annotation { "Feature Type Name" : "Feature", "Feature Type Description" : "" }
export const myFeature = defineFeature(function(context is Context, id is Id, definition is map)
    precondition{}
    {
        {
            var Q0;
            Q0=qCreatedBy(makeId("Top.planeOp"),FACE);
            var sketch = newSketch(context, id + "F0", { "sketchPlane" : qUnion([Q0])});
            skLineSegment(sketch, "E0.bottom", {"start": v(31.75, 56.17) * mm, "end": v(-31.75, 56.17) * mm});
            skLineSegment(sketch, "E0.top", {"start": v(31.75, -56.16) * mm, "end": v(-31.75, -56.16) * mm});
            skLineSegment(sketch, "E0.left", {"start": v(31.75, 56.17) * mm, "end": v(31.75, -56.16) * mm});
            skLineSegment(sketch, "E0.right", {"start": v(-31.75, 56.17) * mm, "end": v(-31.75, -56.16) * mm});
            skPoint(sketch, "E0.middle", {"position": v(0, 0) * mm});
            skCircle(sketch, "E1", {"center": v(0, 33.22) * mm, "radius": 0.46 * mm});
            skLineSegment(sketch, "E2", {"start": v(-15.68, -20.06) * mm, "end": v(-13.05, -16.82) * mm});
            skLineSegment(sketch, "E3", {"start": v(-4.55, -6.35) * mm, "end": v(-4.14, -13.2) * mm});
            skLineSegment(sketch, "E4", {"start": v(-2.74, -36.1) * mm, "end": v(-9.1, -24.2) * mm});
            skLineSegment(sketch, "E5", {"start": v(-20.85, -2.21) * mm, "end": v(7.08, -20.58) * mm});
            skLineSegment(sketch, "E6", {"start": v(7.08, -20.58) * mm, "end": v(-3.54, -22.95) * mm});
            skLineSegment(sketch, "E7", {"start": v(-19.56, -26.53) * mm, "end": v(-15.68, -20.06) * mm});
            skPoint(sketch, "E8.endSnap0", {"position": v(-21.88, 4.12) * mm});
            skLineSegment(sketch, "E9", {"start": v(8.64, -42.82) * mm, "end": v(10.26, -40.5) * mm});
            skLineSegment(sketch, "E10", {"start": v(18.2, -29.11) * mm, "end": v(18.76, -34.8) * mm});
            skLineSegment(sketch, "E11", {"start": v(20.53, -52.9) * mm, "end": v(12.96, -43.77) * mm});
            skLineSegment(sketch, "E12", {"start": v(5.53, -34.8) * mm, "end": v(14.23, -34.8) * mm});
            skLineSegment(sketch, "E13", {"start": v(27.52, -34.8) * mm, "end": v(19.26, -39.9) * mm});
            skLineSegment(sketch, "E14", {"start": v(5.27, -48.51) * mm, "end": v(8.64, -42.82) * mm});
            skText(sketch, "E15", { "text": "QUEEN JANELLE", "fontName": "OpenSans-Regular.ttf"});
            skCircle(sketch, "E16", {"center": v(0, 40.72) * mm, "radius": 7.79 * mm});
            skPoint(sketch, "E17.orphan", {"position": v(-7.14, 4.12) * mm});
            skPoint(sketch, "E18.orphan", {"position": v(-14.42, 0) * mm});
            skPoint(sketch, "E19.orphan", {"position": v(-27.32, -1.7) * mm});
            skPoint(sketch, "E20.start.orphan", {"position": v(-16.45, 9.94) * mm});
            skLineSegment(sketch, "E21", {"start": v(-27.32, -1.7) * mm, "end": v(-21.88, 4.12) * mm});
            skLineSegment(sketch, "E22", {"start": v(-16.45, 9.94) * mm, "end": v(-15.92, 6.43) * mm});
            skLineSegment(sketch, "E23", {"start": v(-14.42, -3.5) * mm, "end": v(-18.7, 0.79) * mm});
            skLineSegment(sketch, "E24", {"start": v(-27.32, 9.43) * mm, "end": v(-18.98, 7.23) * mm});
            skLineSegment(sketch, "E25", {"start": v(-27.32, -1.7) * mm, "end": v(-18.7, 0.79) * mm});
            skLineSegment(sketch, "E26", {"start": v(9.41, -6.35) * mm, "end": v(11.7, -1.56) * mm});
            skLineSegment(sketch, "E27", {"start": v(16.91, 9.43) * mm, "end": v(18.6, 4.51) * mm});
            skLineSegment(sketch, "E28", {"start": v(24.41, -12.3) * mm, "end": v(14, -3.51) * mm});
            skLineSegment(sketch, "E29", {"start": v(4.5, 4.51) * mm, "end": v(14.58, 4.51) * mm});
            skLineSegment(sketch, "E30", {"start": v(27, 4.51) * mm, "end": v(20.08, 0.24) * mm});
            skLineSegment(sketch, "E31.trimOffspring", {"start": v(-18.98, 7.23) * mm, "end": v(-16.45, 9.94) * mm});
            skLineSegment(sketch, "E32.trimOffspring", {"start": v(-15.92, 6.43) * mm, "end": v(-7.14, 4.12) * mm});
            skLineSegment(sketch, "E33.trimOffspring", {"start": v(-15.22, 1.8) * mm, "end": v(-14.42, -3.5) * mm});
            skLineSegment(sketch, "E34.trimOffspring", {"start": v(-15.22, 1.8) * mm, "end": v(-7.14, 4.12) * mm});
            skLineSegment(sketch, "E35.trimOffspring", {"start": v(-21.95, 4.05) * mm, "end": v(-27.32, 9.43) * mm});
            skLineSegment(sketch, "E36.trimOffspring", {"start": v(-13.05, -16.82) * mm, "end": v(-20.85, -2.21) * mm});
            skLineSegment(sketch, "E37.trimOffspring", {"start": v(-8.03, -10.64) * mm, "end": v(-4.55, -6.35) * mm});
            skLineSegment(sketch, "E38.trimOffspring", {"start": v(-3.54, -22.95) * mm, "end": v(-2.74, -36.1) * mm});
            skLineSegment(sketch, "E39.trimOffspring", {"start": v(-9.1, -24.2) * mm, "end": v(-19.56, -26.53) * mm});
            skLineSegment(sketch, "E40.trimOffspring", {"start": v(14.23, -34.8) * mm, "end": v(18.2, -29.11) * mm});
            skLineSegment(sketch, "E41.trimOffspring", {"start": v(18.76, -34.8) * mm, "end": v(27.52, -34.8) * mm});
            skLineSegment(sketch, "E42.trimOffspring", {"start": v(19.26, -39.9) * mm, "end": v(20.53, -52.9) * mm});
            skLineSegment(sketch, "E43.trimOffspring", {"start": v(12.96, -43.77) * mm, "end": v(5.27, -48.51) * mm});
            skLineSegment(sketch, "E44.trimOffspring", {"start": v(10.26, -40.5) * mm, "end": v(5.53, -34.8) * mm});
            skLineSegment(sketch, "E45.trimOffspring", {"start": v(14, -3.51) * mm, "end": v(9.41, -6.35) * mm});
            skLineSegment(sketch, "E46.trimOffspring", {"start": v(18.6, 4.51) * mm, "end": v(27, 4.51) * mm});
            skLineSegment(sketch, "E47.trimOffspring", {"start": v(14.58, 4.51) * mm, "end": v(16.91, 9.43) * mm});
            skLineSegment(sketch, "E48.trimOffspring", {"start": v(20.08, 0.24) * mm, "end": v(24.41, -12.3) * mm});
            skLineSegment(sketch, "E49.trimOffspring", {"start": v(11.7, -1.56) * mm, "end": v(4.5, 4.51) * mm});
            const initialGuessF0  = {"E15": [-0.02986, 0.0172, 1, 0, 0.00585]};
            skSetInitialGuess(sketch, initialGuessF0);
            skSolve(sketch);
        }
        {
            var Q0;
            Q0 = qSketchRegion(id + "F0", true);
            extrude(context, id + "F1", {"entities" : qUnion([Q0]), "depth" : 2 * mm});
        }
        {
            var Q0;
            Q0=makeQuery(id+"F1.opExtrude","CAP_FACE",FACE,{"disambiguationData":[OSD([sQuery(id+"F0.wireOp",EDGE,"E0.bottom"),sQuery(id+"F0.wireOp",EDGE,"E0.top"),sQuery(id+"F0.wireOp",EDGE,"E0.left"),sQuery(id+"F0.wireOp",EDGE,"E0.right"),sQuery(id+"F0.wireOp",EDGE,"E1"),sQuery(id+"F0.wireOp",EDGE,"E2"),sQuery(id+"F0.wireOp",EDGE,"E3"),sQuery(id+"F0.wireOp",EDGE,"E4"),sQuery(id+"F0.wireOp",EDGE,"E5"),sQuery(id+"F0.wireOp",EDGE,"E6"),sQuery(id+"F0.wireOp",EDGE,"E7"),sQuery(id+"F0.wireOp",EDGE,"E9"),sQuery(id+"F0.wireOp",EDGE,"E10"),sQuery(id+"F0.wireOp",EDGE,"E11"),sQuery(id+"F0.wireOp",EDGE,"E12"),sQuery(id+"F0.wireOp",EDGE,"E13"),sQuery(id+"F0.wireOp",EDGE,"E14"),sQuery(id+"F0.wireOp",EDGE,"E15.sketch_text.stroke-0"),sQuery(id+"F0.wireOp",EDGE,"E15.sketch_text.stroke-1"),sQuery(id+"F0.wireOp",EDGE,"E15.sketch_text.stroke-2"),sQuery(id+"F0.wireOp",EDGE,"E15.sketch_text.stroke-3"),sQuery(id+"F0.wireOp",EDGE,"E15.sketch_text.stroke-4"),sQuery(id+"F0.wireOp",EDGE,"E15.sketch_text.stroke-5"),sQuery(id+"F0.wireOp",EDGE,"E15.sketch_text.stroke-6"),sQuery(id+"F0.wireOp",EDGE,"E15.sketch_text.stroke-7"),sQuery(id+"F0.wireOp",EDGE,"E15.sketch_text.stroke-8"),sQuery(id+"F0.wireOp",EDGE,"E15.sketch_text.stroke-9"),sQuery(id+"F0.wireOp",EDGE,"E15.sketch_text.stroke-10"),sQuery(id+"F0.wireOp",EDGE,"E15.sketch_text.stroke-11"),sQuery(id+"F0.wireOp",EDGE,"E15.sketch_text.stroke-20"),sQuery(id+"F0.wireOp",EDGE,"E15.sketch_text.stroke-21"),sQuery(id+"F0.wireOp",EDGE,"E15.sketch_text.stroke-22"),sQuery(id+"F0.wireOp",EDGE,"E15.sketch_text.stroke-23"),sQuery(id+"F0.wireOp",EDGE,"E15.sketch_text.stroke-24"),sQuery(id+"F0.wireOp",EDGE,"E15.sketch_text.stroke-25"),sQuery(id+"F0.wireOp",EDGE,"E15.sketch_text.stroke-26"),sQuery(id+"F0.wireOp",EDGE,"E15.sketch_text.stroke-27"),sQuery(id+"F0.wireOp",EDGE,"E15.sketch_text.stroke-28"),sQuery(id+"F0.wireOp",EDGE,"E15.sketch_text.stroke-29"),sQuery(id+"F0.wireOp",EDGE,"E15.sketch_text.stroke-30"),sQuery(id+"F0.wireOp",EDGE,"E15.sketch_text.stroke-31"),sQuery(id+"F0.wireOp",EDGE,"E15.sketch_text.stroke-32"),sQuery(id+"F0.wireOp",EDGE,"E15.sketch_text.stroke-33"),sQuery(id+"F0.wireOp",EDGE,"E15.sketch_text.stroke-34"),sQuery(id+"F0.wireOp",EDGE,"E15.sketch_text.stroke-35"),sQuery(id+"F0.wireOp",EDGE,"E15.sketch_text.stroke-36"),sQuery(id+"F0.wireOp",EDGE,"E15.sketch_text.stroke-37"),sQuery(id+"F0.wireOp",EDGE,"E15.sketch_text.stroke-38"),sQuery(id+"F0.wireOp",EDGE,"E15.sketch_text.stroke-39"),sQuery(id+"F0.wireOp",EDGE,"E15.sketch_text.stroke-40"),sQuery(id+"F0.wireOp",EDGE,"E15.sketch_text.stroke-41"),sQuery(id+"F0.wireOp",EDGE,"E15.sketch_text.stroke-42"),sQuery(id+"F0.wireOp",EDGE,"E15.sketch_text.stroke-43"),sQuery(id+"F0.wireOp",EDGE,"E15.sketch_text.stroke-44"),sQuery(id+"F0.wireOp",EDGE,"E15.sketch_text.stroke-45"),sQuery(id+"F0.wireOp",EDGE,"E15.sketch_text.stroke-46"),sQuery(id+"F0.wireOp",EDGE,"E15.sketch_text.stroke-47"),sQuery(id+"F0.wireOp",EDGE,"E15.sketch_text.stroke-48"),sQuery(id+"F0.wireOp",EDGE,"E15.sketch_text.stroke-49"),sQuery(id+"F0.wireOp",EDGE,"E15.sketch_text.stroke-50"),sQuery(id+"F0.wireOp",EDGE,"E15.sketch_text.stroke-51"),sQuery(id+"F0.wireOp",EDGE,"E15.sketch_text.stroke-52"),sQuery(id+"F0.wireOp",EDGE,"E15.sketch_text.stroke-53"),sQuery(id+"F0.wireOp",EDGE,"E15.sketch_text.stroke-54"),sQuery(id+"F0.wireOp",EDGE,"E15.sketch_text.stroke-55"),sQuery(id+"F0.wireOp",EDGE,"E15.sketch_text.stroke-56"),sQuery(id+"F0.wireOp",EDGE,"E15.sketch_text.stroke-57"),sQuery(id+"F0.wireOp",EDGE,"E15.sketch_text.stroke-58"),sQuery(id+"F0.wireOp",EDGE,"E15.sketch_text.stroke-59"),sQuery(id+"F0.wireOp",EDGE,"E15.sketch_text.stroke-60"),sQuery(id+"F0.wireOp",EDGE,"E15.sketch_text.stroke-61"),sQuery(id+"F0.wireOp",EDGE,"E15.sketch_text.stroke-62"),sQuery(id+"F0.wireOp",EDGE,"E15.sketch_text.stroke-63"),sQuery(id+"F0.wireOp",EDGE,"E15.sketch_text.stroke-64"),sQuery(id+"F0.wireOp",EDGE,"E15.sketch_text.stroke-65"),sQuery(id+"F0.wireOp",EDGE,"E15.sketch_text.stroke-66"),sQuery(id+"F0.wireOp",EDGE,"E15.sketch_text.stroke-67"),sQuery(id+"F0.wireOp",EDGE,"E15.sketch_text.stroke-68"),sQuery(id+"F0.wireOp",EDGE,"E15.sketch_text.stroke-69"),sQuery(id+"F0.wireOp",EDGE,"E15.sketch_text.stroke-70"),sQuery(id+"F0.wireOp",EDGE,"E15.sketch_text.stroke-71"),sQuery(id+"F0.wireOp",EDGE,"E15.sketch_text.stroke-72"),sQuery(id+"F0.wireOp",EDGE,"E15.sketch_text.stroke-73"),sQuery(id+"F0.wireOp",EDGE,"E15.sketch_text.stroke-74"),sQuery(id+"F0.wireOp",EDGE,"E15.sketch_text.stroke-75"),sQuery(id+"F0.wireOp",EDGE,"E15.sketch_text.stroke-76"),sQuery(id+"F0.wireOp",EDGE,"E15.sketch_text.stroke-77"),sQuery(id+"F0.wireOp",EDGE,"E15.sketch_text.stroke-78"),sQuery(id+"F0.wireOp",EDGE,"E15.sketch_text.stroke-79"),sQuery(id+"F0.wireOp",EDGE,"E15.sketch_text.stroke-80"),sQuery(id+"F0.wireOp",EDGE,"E15.sketch_text.stroke-81"),sQuery(id+"F0.wireOp",EDGE,"E15.sketch_text.stroke-82"),sQuery(id+"F0.wireOp",EDGE,"E15.sketch_text.stroke-83"),sQuery(id+"F0.wireOp",EDGE,"E15.sketch_text.stroke-84"),sQuery(id+"F0.wireOp",EDGE,"E15.sketch_text.stroke-85"),sQuery(id+"F0.wireOp",EDGE,"E15.sketch_text.stroke-86"),sQuery(id+"F0.wireOp",EDGE,"E15.sketch_text.stroke-87"),sQuery(id+"F0.wireOp",EDGE,"E15.sketch_text.stroke-88"),sQuery(id+"F0.wireOp",EDGE,"E15.sketch_text.stroke-89"),sQuery(id+"F0.wireOp",EDGE,"E15.sketch_text.stroke-90"),sQuery(id+"F0.wireOp",EDGE,"E15.sketch_text.stroke-96"),sQuery(id+"F0.wireOp",EDGE,"E15.sketch_text.stroke-97"),sQuery(id+"F0.wireOp",EDGE,"E15.sketch_text.stroke-98"),sQuery(id+"F0.wireOp",EDGE,"E15.sketch_text.stroke-99"),sQuery(id+"F0.wireOp",EDGE,"E15.sketch_text.stroke-100"),sQuery(id+"F0.wireOp",EDGE,"E15.sketch_text.stroke-101"),sQuery(id+"F0.wireOp",EDGE,"E15.sketch_text.stroke-102"),sQuery(id+"F0.wireOp",EDGE,"E15.sketch_text.stroke-103"),sQuery(id+"F0.wireOp",EDGE,"E15.sketch_text.stroke-104"),sQuery(id+"F0.wireOp",EDGE,"E15.sketch_text.stroke-105"),sQuery(id+"F0.wireOp",EDGE,"E15.sketch_text.stroke-106"),sQuery(id+"F0.wireOp",EDGE,"E15.sketch_text.stroke-107"),sQuery(id+"F0.wireOp",EDGE,"E15.sketch_text.stroke-108"),sQuery(id+"F0.wireOp",EDGE,"E15.sketch_text.stroke-109"),sQuery(id+"F0.wireOp",EDGE,"E15.sketch_text.stroke-110"),sQuery(id+"F0.wireOp",EDGE,"E15.sketch_text.stroke-111"),sQuery(id+"F0.wireOp",EDGE,"E15.sketch_text.stroke-112"),sQuery(id+"F0.wireOp",EDGE,"E15.sketch_text.stroke-113"),sQuery(id+"F0.wireOp",EDGE,"E15.sketch_text.stroke-114"),sQuery(id+"F0.wireOp",EDGE,"E15.sketch_text.stroke-115"),sQuery(id+"F0.wireOp",EDGE,"E15.sketch_text.stroke-116"),sQuery(id+"F0.wireOp",EDGE,"E15.sketch_text.stroke-117"),sQuery(id+"F0.wireOp",EDGE,"E15.sketch_text.stroke-118"),sQuery(id+"F0.wireOp",EDGE,"E15.sketch_text.stroke-119"),sQuery(id+"F0.wireOp",EDGE,"E15.sketch_text.stroke-120"),sQuery(id+"F0.wireOp",EDGE,"E15.sketch_text.stroke-121"),sQuery(id+"F0.wireOp",EDGE,"E15.sketch_text.stroke-122"),sQuery(id+"F0.wireOp",EDGE,"E15.sketch_text.stroke-123"),sQuery(id+"F0.wireOp",EDGE,"E15.sketch_text.stroke-124"),sQuery(id+"F0.wireOp",EDGE,"E15.sketch_text.stroke-125"),sQuery(id+"F0.wireOp",EDGE,"E15.sketch_text.stroke-126"),sQuery(id+"F0.wireOp",EDGE,"E15.sketch_text.stroke-127"),sQuery(id+"F0.wireOp",EDGE,"E15.sketch_text.stroke-128"),sQuery(id+"F0.wireOp",EDGE,"E15.sketch_text.stroke-129"),sQuery(id+"F0.wireOp",EDGE,"E15.sketch_text.stroke-130"),sQuery(id+"F0.wireOp",EDGE,"E15.sketch_text.stroke-131"),sQuery(id+"F0.wireOp",EDGE,"E15.sketch_text.stroke-132"),sQuery(id+"F0.wireOp",EDGE,"E15.sketch_text.stroke-133"),sQuery(id+"F0.wireOp",EDGE,"E15.sketch_text.stroke-134"),sQuery(id+"F0.wireOp",EDGE,"E15.sketch_text.stroke-135"),sQuery(id+"F0.wireOp",EDGE,"E15.sketch_text.stroke-136"),sQuery(id+"F0.wireOp",EDGE,"E15.sketch_text.stroke-137"),sQuery(id+"F0.wireOp",EDGE,"E15.sketch_text.stroke-138"),sQuery(id+"F0.wireOp",EDGE,"E15.sketch_text.stroke-139"),sQuery(id+"F0.wireOp",EDGE,"E15.sketch_text.stroke-140"),sQuery(id+"F0.wireOp",EDGE,"E15.sketch_text.stroke-141"),sQuery(id+"F0.wireOp",EDGE,"E15.sketch_text.stroke-142"),sQuery(id+"F0.wireOp",EDGE,"E15.sketch_text.stroke-143"),sQuery(id+"F0.wireOp",EDGE,"E15.sketch_text.stroke-144"),sQuery(id+"F0.wireOp",EDGE,"E15.sketch_text.stroke-145"),sQuery(id+"F0.wireOp",EDGE,"E15.sketch_text.stroke-146"),sQuery(id+"F0.wireOp",EDGE,"E16"),sQuery(id+"F0.wireOp",EDGE,"E21"),sQuery(id+"F0.wireOp",EDGE,"E22"),sQuery(id+"F0.wireOp",EDGE,"E23"),sQuery(id+"F0.wireOp",EDGE,"E24"),sQuery(id+"F0.wireOp",EDGE,"E25"),sQuery(id+"F0.wireOp",EDGE,"E26"),sQuery(id+"F0.wireOp",EDGE,"E27"),sQuery(id+"F0.wireOp",EDGE,"E28"),sQuery(id+"F0.wireOp",EDGE,"E29"),sQuery(id+"F0.wireOp",EDGE,"E30"),sQuery(id+"F0.wireOp",EDGE,"E31.trimOffspring"),sQuery(id+"F0.wireOp",EDGE,"E32.trimOffspring"),sQuery(id+"F0.wireOp",EDGE,"E33.trimOffspring"),sQuery(id+"F0.wireOp",EDGE,"E34.trimOffspring"),sQuery(id+"F0.wireOp",EDGE,"E35.trimOffspring"),sQuery(id+"F0.wireOp",EDGE,"E36.trimOffspring"),sQuery(id+"F0.wireOp",EDGE,"E37.trimOffspring"),sQuery(id+"F0.wireOp",EDGE,"E38.trimOffspring"),sQuery(id+"F0.wireOp",EDGE,"E39.trimOffspring"),sQuery(id+"F0.wireOp",EDGE,"E40.trimOffspring"),sQuery(id+"F0.wireOp",EDGE,"E41.trimOffspring"),sQuery(id+"F0.wireOp",EDGE,"E42.trimOffspring"),sQuery(id+"F0.wireOp",EDGE,"E43.trimOffspring"),sQuery(id+"F0.wireOp",EDGE,"E44.trimOffspring"),sQuery(id+"F0.wireOp",EDGE,"E45.trimOffspring"),sQuery(id+"F0.wireOp",EDGE,"E46.trimOffspring"),sQuery(id+"F0.wireOp",EDGE,"E47.trimOffspring"),sQuery(id+"F0.wireOp",EDGE,"E48.trimOffspring"),sQuery(id+"F0.wireOp",EDGE,"E49.trimOffspring")])],"isStart":true});
            var sketch = newSketch(context, id + "F2", { "sketchPlane" : qUnion([Q0])});
            skLineSegment(sketch, "E50.top", {"start": v(-31.75, -57.77) * mm, "end": v(-33.35, -57.77) * mm});
            skLineSegment(sketch, "E50.left", {"start": v(-31.75, 56.16) * mm, "end": v(-31.75, -56.17) * mm});
            skLineSegment(sketch, "E50.right", {"start": v(-33.35, 56.16) * mm, "end": v(-33.35, -57.77) * mm});
            skLineSegment(sketch, "E51.bottom", {"start": v(-33.35, -57.77) * mm, "end": v(33.35, -57.77) * mm});
            skLineSegment(sketch, "E51.top", {"start": v(-31.75, -56.17) * mm, "end": v(31.75, -56.17) * mm});
            skLineSegment(sketch, "E51.left", {"start": v(-33.35, -57.77) * mm, "end": v(-33.35, -56.17) * mm});
            skLineSegment(sketch, "E51.right", {"start": v(33.35, -57.77) * mm, "end": v(33.35, -56.17) * mm});
            skLineSegment(sketch, "E52.top", {"start": v(33.35, -57.77) * mm, "end": v(31.75, -57.77) * mm});
            skLineSegment(sketch, "E52.left", {"start": v(33.35, 56.17) * mm, "end": v(33.35, -57.77) * mm});
            skLineSegment(sketch, "E52.right", {"start": v(31.75, 56.16) * mm, "end": v(31.75, -56.17) * mm});
            skLineSegment(sketch, "E53.bottom", {"start": v(31.75, 56.16) * mm, "end": v(-31.75, 56.16) * mm});
            skLineSegment(sketch, "E53.top", {"start": v(33.35, 57.77) * mm, "end": v(-33.35, 57.76) * mm});
            skLineSegment(sketch, "E53.left", {"start": v(33.35, 56.17) * mm, "end": v(33.35, 57.77) * mm});
            skLineSegment(sketch, "E53.right", {"start": v(-33.35, 56.16) * mm, "end": v(-33.35, 57.76) * mm});
            skSolve(sketch);
        }
        {
            var Q0;
            Q0 = qSketchRegion(id + "F2", true);
            extrude(context, id + "F3", {"entities" : qUnion([Q0]), "operationType" : NewBodyOperationType.ADD, "depth" : 14 * mm, "hasSecondDirection" : true, "secondDirectionOppositeDirection" : true, "secondDirectionDepth" : 2 * mm});
        }
        {
            var Q0;
            Q0=makeQuery(id+"F3.opExtrude","CAP_EDGE",EDGE,{"disambiguationData":[OSD([sQuery(id+"F2.wireOp",EDGE,"E53.top")])],"isStart":true});
            var Q1;
            Q1=makeQuery(id+"F3.opExtrude","CAP_EDGE",EDGE,{"disambiguationData":[OSD([sQuery(id+"F2.wireOp",EDGE,"E52.left"),sQuery(id+"F2.wireOp",EDGE,"E53.left")])],"isStart":true});
            var Q2;
            Q2=makeQuery(id+"F3.opExtrude","CAP_EDGE",EDGE,{"disambiguationData":[OSD([sQuery(id+"F2.wireOp",EDGE,"E51.bottom"),sQuery(id+"F2.wireOp",EDGE,"E52.top")])],"isStart":true});
            var Q3;
            Q3=makeQuery(id+"F3.opExtrude","CAP_EDGE",EDGE,{"disambiguationData":[OSD([sQuery(id+"F2.wireOp",EDGE,"E50.right"),sQuery(id+"F2.wireOp",EDGE,"E51.left"),sQuery(id+"F2.wireOp",EDGE,"E53.right")])],"isStart":true});
            fillet(context, id + "F4", {"entities" : qUnion([Q0, Q1, Q2, Q3]), "radius" : 6 * mm, "tangentPropagation" : true, "allowEdgeOverflow" : false});
        }
        {
            var Q0;
            Q0=makeQuery(id+"F3.opExtrude","SWEPT_EDGE",EDGE,{"disambiguationData":[OSD([sQuery(id+"F2.wireOp",EDGE,"E52.right"),sQuery(id+"F2.wireOp",EDGE,"E53.bottom")])]});
            var Q1;
            Q1=makeQuery(id+"F3.opExtrude","SWEPT_EDGE",EDGE,{"disambiguationData":[OSD([sQuery(id+"F2.wireOp",EDGE,"E50.left"),sQuery(id+"F2.wireOp",EDGE,"E53.bottom")])]});
            var Q2;
            Q2=makeQuery(id+"F3.opExtrude","SWEPT_EDGE",EDGE,{"disambiguationData":[OSD([sQuery(id+"F2.wireOp",EDGE,"E51.top"),sQuery(id+"F2.wireOp",EDGE,"E52.right")])]});
            var Q3;
            Q3=makeQuery(id+"F3.opExtrude","SWEPT_EDGE",EDGE,{"disambiguationData":[OSD([sQuery(id+"F2.wireOp",EDGE,"E50.left"),sQuery(id+"F2.wireOp",EDGE,"E51.top")])]});
            fillet(context, id + "F5", {"entities" : qUnion([Q0, Q1, Q2, Q3]), "radius" : 6.94 * mm, "tangentPropagation" : true, "allowEdgeOverflow" : false});
        }
        {
            var Q0;
            Q0=makeQuery(id+"F3.opExtrude","SWEPT_EDGE",EDGE,{"disambiguationData":[OSD([sQuery(id+"F2.wireOp",EDGE,"E51.bottom"),sQuery(id+"F2.wireOp",EDGE,"E51.left")])]});
            var Q1;
            Q1=makeQuery(id+"F3.opExtrude","SWEPT_EDGE",EDGE,{"disambiguationData":[OSD([sQuery(id+"F2.wireOp",EDGE,"E52.top"),sQuery(id+"F2.wireOp",EDGE,"E52.left")])]});
            var Q2;
            Q2=makeQuery(id+"F3.opExtrude","SWEPT_EDGE",EDGE,{"disambiguationData":[OSD([sQuery(id+"F2.wireOp",EDGE,"E53.top"),sQuery(id+"F2.wireOp",EDGE,"E53.right")])]});
            var Q3;
            Q3=makeQuery(id+"F3.opExtrude","SWEPT_EDGE",EDGE,{"disambiguationData":[OSD([sQuery(id+"F2.wireOp",EDGE,"E53.top"),sQuery(id+"F2.wireOp",EDGE,"E53.left")])]});
            fillet(context, id + "F6", {"entities" : qUnion([Q0, Q1, Q2, Q3]), "radius" : 7.82 * mm, "tangentPropagation" : true, "allowEdgeOverflow" : false});
        }
        {
            var Q0;
            Q0=makeQuery(id+"F3.opExtrude","SWEPT_FACE",FACE,{"disambiguationData":[OSD([sQuery(id+"F2.wireOp",EDGE,"E53.top")])]});
            var sketch = newSketch(context, id + "F7", { "sketchPlane" : qUnion([Q0])});
            skLineSegment(sketch, "E54.bottom", {"start": v(-10.28, -10.15) * mm, "end": v(10.28, -10.15) * mm});
            skLineSegment(sketch, "E54.top", {"start": v(-10.28, -5.01) * mm, "end": v(10.28, -5.01) * mm});
            skLineSegment(sketch, "E54.left", {"start": v(-10.28, -10.15) * mm, "end": v(-10.28, -5.01) * mm});
            skLineSegment(sketch, "E54.right", {"start": v(10.28, -10.15) * mm, "end": v(10.28, -5.01) * mm});
            skPoint(sketch, "E54.middle", {"position": v(0, -7.58) * mm});
            skSolve(sketch);
        }
        {
            var Q0;
            Q0=makeQuery(id+"F7.imprint","IMPRINT",FACE,{"disambiguationData":[TD([[makeQuery(id+"F7.imprint","IMPRINT",EDGE,{"derivedFrom":sQuery(id+"F7.wireOp",EDGE,"E54.bottom")}),1.0]])]});
            extrude(context, id + "F8", {"entities" : qUnion([Q0]), "operationType" : NewBodyOperationType.REMOVE, "oppositeDirection" : true, "depth" : 3 * mm});
        }
        {
            var Q0;
            Q0=makeQuery(id+"F3.opExtrude","SWEPT_FACE",FACE,{"disambiguationData":[OSD([sQuery(id+"F2.wireOp",EDGE,"E52.left"),sQuery(id+"F2.wireOp",EDGE,"E53.left")])]});
            var sketch = newSketch(context, id + "F9", { "sketchPlane" : qUnion([Q0])});
            skLineSegment(sketch, "E55", {"start": v(-27.94, -4) * mm, "end": v(-27.94, -28.75) * mm, "construction": true});
            skLineSegment(sketch, "E56.bottom", {"start": v(-27.94, -4) * mm, "end": v(-4.11, -4) * mm});
            skLineSegment(sketch, "E56.top", {"start": v(-27.94, -9.9) * mm, "end": v(-4.11, -9.9) * mm});
            skLineSegment(sketch, "E56.left", {"start": v(-27.94, -4) * mm, "end": v(-27.94, -9.9) * mm});
            skLineSegment(sketch, "E56.right", {"start": v(-4.11, -4) * mm, "end": v(-4.11, -9.9) * mm});
            skSolve(sketch);
        }
        {
            var Q0;
            Q0 = qSketchRegion(id + "F9", true);
            extrude(context, id + "F10", {"entities" : qUnion([Q0]), "operationType" : NewBodyOperationType.REMOVE, "oppositeDirection" : true, "depth" : 3 * mm});
        }
        {
            var Q0;
            Q0=makeQuery(id+"F3.opExtrude","CAP_EDGE",EDGE,{"disambiguationData":[OSD([sQuery(id+"F2.wireOp",EDGE,"E51.bottom"),sQuery(id+"F2.wireOp",EDGE,"E52.top")])],"isStart":false});
            fillet(context, id + "F11", {"entities" : qUnion([Q0]), "radius" : 0.02 * mm, "tangentPropagation" : true, "allowEdgeOverflow" : false});
        }
        {
            var Q0;
            Q0=makeQuery(id+"F3.opExtrude","SWEPT_FACE",FACE,{"disambiguationData":[OSD([sQuery(id+"F2.wireOp",EDGE,"E52.right")])]});
            var sketch = newSketch(context, id + "F12", { "sketchPlane" : qUnion([Q0])});
            skLineSegment(sketch, "E57.bottom", {"start": v(49.23, -14) * mm, "end": v(-49.23, -14) * mm});
            skLineSegment(sketch, "E57.top", {"start": v(49.23, -12) * mm, "end": v(-49.23, -12) * mm});
            skLineSegment(sketch, "E57.left", {"start": v(49.23, -14) * mm, "end": v(49.23, -12) * mm});
            skLineSegment(sketch, "E57.right", {"start": v(-49.23, -14) * mm, "end": v(-49.23, -12) * mm});
            skSolve(sketch);
        }
        {
            var Q0;
            Q0 = qSketchRegion(id + "F12", true);
            extrude(context, id + "F13", {"entities" : qUnion([Q0]), "operationType" : NewBodyOperationType.ADD, "depth" : 3 * mm});
        }
        {
            var Q0;
            Q0=makeQuery(id+"F13.opExtrude","CAP_EDGE",EDGE,{"disambiguationData":[OSD([sQuery(id+"F12.wireOp",EDGE,"E57.left")])],"isStart":false});
            var Q1;
            Q1=makeQuery(id+"F13.opExtrude","CAP_EDGE",EDGE,{"disambiguationData":[OSD([sQuery(id+"F12.wireOp",EDGE,"E57.right")])],"isStart":false});
            chamfer(context, id + "F14", {"entities" : qUnion([Q0, Q1]), "chamferType" : ChamferType.OFFSET_ANGLE, "width" : 3 * mm, "oppositeDirection" : false, "angle" : 45 * degree});
        }
        {
            var Q0;
            Q0=makeQuery(id+"F3.opExtrude","SWEPT_FACE",FACE,{"disambiguationData":[OSD([sQuery(id+"F2.wireOp",EDGE,"E50.left")])]});
            var sketch = newSketch(context, id + "F15", { "sketchPlane" : qUnion([Q0])});
            skLineSegment(sketch, "E58.bottom", {"start": v(49.23, -14) * mm, "end": v(-49.23, -14) * mm});
            skLineSegment(sketch, "E58.top", {"start": v(49.23, -12) * mm, "end": v(-49.23, -12) * mm});
            skLineSegment(sketch, "E58.left", {"start": v(49.23, -14) * mm, "end": v(49.23, -12) * mm});
            skLineSegment(sketch, "E58.right", {"start": v(-49.23, -14) * mm, "end": v(-49.23, -12) * mm});
            skSolve(sketch);
        }
        {
            var Q0;
            Q0=makeQuery(id+"F15.imprint","IMPRINT",FACE,{"disambiguationData":[TD([[makeQuery(id+"F15.imprint","IMPRINT",EDGE,{"derivedFrom":sQuery(id+"F15.wireOp",EDGE,"E58.bottom")}),-1.0]])]});
            extrude(context, id + "F16", {"entities" : qUnion([Q0]), "operationType" : NewBodyOperationType.ADD, "depth" : 3 * mm});
        }
        {
            var Q0;
            Q0=makeQuery(id+"F16.opExtrude","CAP_EDGE",EDGE,{"disambiguationData":[OSD([sQuery(id+"F15.wireOp",EDGE,"E58.left")])],"isStart":false});
            var Q1;
            Q1=makeQuery(id+"F16.opExtrude","CAP_EDGE",EDGE,{"disambiguationData":[OSD([sQuery(id+"F15.wireOp",EDGE,"E58.right")])],"isStart":false});
            fillet(context, id + "F17", {"entities" : qUnion([Q0, Q1]), "radius" : 44 * mm, "tangentPropagation" : true, "allowEdgeOverflow" : false});
        }
        {
            var Q0;
            Q0=makeQuery(id+"F3.opExtrude","SWEPT_FACE",FACE,{"disambiguationData":[OSD([sQuery(id+"F2.wireOp",EDGE,"E51.top")])]});
            var sketch = newSketch(context, id + "F18", { "sketchPlane" : qUnion([Q0])});
            skLineSegment(sketch, "E59.bottom", {"start": v(-24.81, -14) * mm, "end": v(24.81, -14) * mm});
            skLineSegment(sketch, "E59.top", {"start": v(-24.81, -12) * mm, "end": v(24.81, -12) * mm});
            skLineSegment(sketch, "E59.left", {"start": v(-24.81, -14) * mm, "end": v(-24.81, -12) * mm});
            skLineSegment(sketch, "E59.right", {"start": v(24.81, -14) * mm, "end": v(24.81, -12) * mm});
            skSolve(sketch);
        }
        {
            var Q0;
            Q0 = qSketchRegion(id + "F18", true);
            extrude(context, id + "F19", {"entities" : qUnion([Q0]), "operationType" : NewBodyOperationType.ADD, "depth" : 2 * mm});
        }
        {
            var Q0;
            Q0=makeQuery(id+"F19.opExtrude","CAP_EDGE",EDGE,{"disambiguationData":[OSD([sQuery(id+"F18.wireOp",EDGE,"E59.left")])],"isStart":false});
            var Q1;
            Q1=makeQuery(id+"F19.opExtrude","CAP_EDGE",EDGE,{"disambiguationData":[OSD([sQuery(id+"F18.wireOp",EDGE,"E59.right")])],"isStart":false});
            fillet(context, id + "F20", {"entities" : qUnion([Q0, Q1]), "radius" : 44 * mm, "tangentPropagation" : true, "allowEdgeOverflow" : false});
        }
        {
            var Q0;
            Q0=makeQuery(id+"F3.opExtrude","SWEPT_FACE",FACE,{"disambiguationData":[OSD([sQuery(id+"F2.wireOp",EDGE,"E53.bottom")])]});
            var sketch = newSketch(context, id + "F21", { "sketchPlane" : qUnion([Q0])});
            skLineSegment(sketch, "E60.bottom", {"start": v(24.81, -14) * mm, "end": v(-24.81, -14) * mm});
            skLineSegment(sketch, "E60.top", {"start": v(24.81, -12) * mm, "end": v(-24.81, -12) * mm});
            skLineSegment(sketch, "E60.left", {"start": v(24.81, -14) * mm, "end": v(24.81, -12) * mm});
            skLineSegment(sketch, "E60.right", {"start": v(-24.81, -14) * mm, "end": v(-24.81, -12) * mm});
            skSolve(sketch);
        }
        {
            var Q0;
            Q0 = qSketchRegion(id + "F21", true);
            extrude(context, id + "F22", {"entities" : qUnion([Q0]), "operationType" : NewBodyOperationType.ADD, "depth" : 2 * mm});
        }
        {
            var Q0;
            Q0=makeQuery(id+"F22.opExtrude","CAP_EDGE",EDGE,{"disambiguationData":[OSD([sQuery(id+"F21.wireOp",EDGE,"E60.left")])],"isStart":false});
            var Q1;
            Q1=makeQuery(id+"F22.opExtrude","CAP_EDGE",EDGE,{"disambiguationData":[OSD([sQuery(id+"F21.wireOp",EDGE,"E60.right")])],"isStart":false});
            fillet(context, id + "F23", {"entities" : qUnion([Q0, Q1]), "radius" : 175.27 * mm, "tangentPropagation" : true, "allowEdgeOverflow" : false});
        }
        {
            var Q0;
            Q0=makeQuery(id+"F4.opFillet","SPLIT",FACE,{"disambiguationData":[OD(1.0)],"derivedFrom":makeQuery(id+"F3.boolean.opBoolean","MERGE",FACE,{"derivedFrom":[makeQuery(id+"F1.opExtrude","CAP_FACE",FACE,{"disambiguationData":[OSD([sQuery(id+"F0.wireOp",EDGE,"E0.bottom"),sQuery(id+"F0.wireOp",EDGE,"E0.top"),sQuery(id+"F0.wireOp",EDGE,"E0.left"),sQuery(id+"F0.wireOp",EDGE,"E0.right"),sQuery(id+"F0.wireOp",EDGE,"E1"),sQuery(id+"F0.wireOp",EDGE,"E2"),sQuery(id+"F0.wireOp",EDGE,"E3"),sQuery(id+"F0.wireOp",EDGE,"E4"),sQuery(id+"F0.wireOp",EDGE,"E5"),sQuery(id+"F0.wireOp",EDGE,"E6"),sQuery(id+"F0.wireOp",EDGE,"E7"),sQuery(id+"F0.wireOp",EDGE,"E9"),sQuery(id+"F0.wireOp",EDGE,"E10"),sQuery(id+"F0.wireOp",EDGE,"E11"),sQuery(id+"F0.wireOp",EDGE,"E12"),sQuery(id+"F0.wireOp",EDGE,"E13"),sQuery(id+"F0.wireOp",EDGE,"E14"),sQuery(id+"F0.wireOp",EDGE,"E15.sketch_text.stroke-0"),sQuery(id+"F0.wireOp",EDGE,"E15.sketch_text.stroke-1"),sQuery(id+"F0.wireOp",EDGE,"E15.sketch_text.stroke-2"),sQuery(id+"F0.wireOp",EDGE,"E15.sketch_text.stroke-3"),sQuery(id+"F0.wireOp",EDGE,"E15.sketch_text.stroke-4"),sQuery(id+"F0.wireOp",EDGE,"E15.sketch_text.stroke-5"),sQuery(id+"F0.wireOp",EDGE,"E15.sketch_text.stroke-6"),sQuery(id+"F0.wireOp",EDGE,"E15.sketch_text.stroke-7"),sQuery(id+"F0.wireOp",EDGE,"E15.sketch_text.stroke-8"),sQuery(id+"F0.wireOp",EDGE,"E15.sketch_text.stroke-9"),sQuery(id+"F0.wireOp",EDGE,"E15.sketch_text.stroke-10"),sQuery(id+"F0.wireOp",EDGE,"E15.sketch_text.stroke-11"),sQuery(id+"F0.wireOp",EDGE,"E15.sketch_text.stroke-20"),sQuery(id+"F0.wireOp",EDGE,"E15.sketch_text.stroke-21"),sQuery(id+"F0.wireOp",EDGE,"E15.sketch_text.stroke-22"),sQuery(id+"F0.wireOp",EDGE,"E15.sketch_text.stroke-23"),sQuery(id+"F0.wireOp",EDGE,"E15.sketch_text.stroke-24"),sQuery(id+"F0.wireOp",EDGE,"E15.sketch_text.stroke-25"),sQuery(id+"F0.wireOp",EDGE,"E15.sketch_text.stroke-26"),sQuery(id+"F0.wireOp",EDGE,"E15.sketch_text.stroke-27"),sQuery(id+"F0.wireOp",EDGE,"E15.sketch_text.stroke-28"),sQuery(id+"F0.wireOp",EDGE,"E15.sketch_text.stroke-29"),sQuery(id+"F0.wireOp",EDGE,"E15.sketch_text.stroke-30"),sQuery(id+"F0.wireOp",EDGE,"E15.sketch_text.stroke-31"),sQuery(id+"F0.wireOp",EDGE,"E15.sketch_text.stroke-32"),sQuery(id+"F0.wireOp",EDGE,"E15.sketch_text.stroke-33"),sQuery(id+"F0.wireOp",EDGE,"E15.sketch_text.stroke-34"),sQuery(id+"F0.wireOp",EDGE,"E15.sketch_text.stroke-35"),sQuery(id+"F0.wireOp",EDGE,"E15.sketch_text.stroke-36"),sQuery(id+"F0.wireOp",EDGE,"E15.sketch_text.stroke-37"),sQuery(id+"F0.wireOp",EDGE,"E15.sketch_text.stroke-38"),sQuery(id+"F0.wireOp",EDGE,"E15.sketch_text.stroke-39"),sQuery(id+"F0.wireOp",EDGE,"E15.sketch_text.stroke-40"),sQuery(id+"F0.wireOp",EDGE,"E15.sketch_text.stroke-41"),sQuery(id+"F0.wireOp",EDGE,"E15.sketch_text.stroke-42"),sQuery(id+"F0.wireOp",EDGE,"E15.sketch_text.stroke-43"),sQuery(id+"F0.wireOp",EDGE,"E15.sketch_text.stroke-44"),sQuery(id+"F0.wireOp",EDGE,"E15.sketch_text.stroke-45"),sQuery(id+"F0.wireOp",EDGE,"E15.sketch_text.stroke-46"),sQuery(id+"F0.wireOp",EDGE,"E15.sketch_text.stroke-47"),sQuery(id+"F0.wireOp",EDGE,"E15.sketch_text.stroke-48"),sQuery(id+"F0.wireOp",EDGE,"E15.sketch_text.stroke-49"),sQuery(id+"F0.wireOp",EDGE,"E15.sketch_text.stroke-50"),sQuery(id+"F0.wireOp",EDGE,"E15.sketch_text.stroke-51"),sQuery(id+"F0.wireOp",EDGE,"E15.sketch_text.stroke-52"),sQuery(id+"F0.wireOp",EDGE,"E15.sketch_text.stroke-53"),sQuery(id+"F0.wireOp",EDGE,"E15.sketch_text.stroke-54"),sQuery(id+"F0.wireOp",EDGE,"E15.sketch_text.stroke-55"),sQuery(id+"F0.wireOp",EDGE,"E15.sketch_text.stroke-56"),sQuery(id+"F0.wireOp",EDGE,"E15.sketch_text.stroke-57"),sQuery(id+"F0.wireOp",EDGE,"E15.sketch_text.stroke-58"),sQuery(id+"F0.wireOp",EDGE,"E15.sketch_text.stroke-59"),sQuery(id+"F0.wireOp",EDGE,"E15.sketch_text.stroke-60"),sQuery(id+"F0.wireOp",EDGE,"E15.sketch_text.stroke-61"),sQuery(id+"F0.wireOp",EDGE,"E15.sketch_text.stroke-62"),sQuery(id+"F0.wireOp",EDGE,"E15.sketch_text.stroke-63"),sQuery(id+"F0.wireOp",EDGE,"E15.sketch_text.stroke-64"),sQuery(id+"F0.wireOp",EDGE,"E15.sketch_text.stroke-65"),sQuery(id+"F0.wireOp",EDGE,"E15.sketch_text.stroke-66"),sQuery(id+"F0.wireOp",EDGE,"E15.sketch_text.stroke-67"),sQuery(id+"F0.wireOp",EDGE,"E15.sketch_text.stroke-68"),sQuery(id+"F0.wireOp",EDGE,"E15.sketch_text.stroke-69"),sQuery(id+"F0.wireOp",EDGE,"E15.sketch_text.stroke-70"),sQuery(id+"F0.wireOp",EDGE,"E15.sketch_text.stroke-71"),sQuery(id+"F0.wireOp",EDGE,"E15.sketch_text.stroke-72"),sQuery(id+"F0.wireOp",EDGE,"E15.sketch_text.stroke-73"),sQuery(id+"F0.wireOp",EDGE,"E15.sketch_text.stroke-74"),sQuery(id+"F0.wireOp",EDGE,"E15.sketch_text.stroke-75"),sQuery(id+"F0.wireOp",EDGE,"E15.sketch_text.stroke-76"),sQuery(id+"F0.wireOp",EDGE,"E15.sketch_text.stroke-77"),sQuery(id+"F0.wireOp",EDGE,"E15.sketch_text.stroke-78"),sQuery(id+"F0.wireOp",EDGE,"E15.sketch_text.stroke-79"),sQuery(id+"F0.wireOp",EDGE,"E15.sketch_text.stroke-80"),sQuery(id+"F0.wireOp",EDGE,"E15.sketch_text.stroke-81"),sQuery(id+"F0.wireOp",EDGE,"E15.sketch_text.stroke-82"),sQuery(id+"F0.wireOp",EDGE,"E15.sketch_text.stroke-83"),sQuery(id+"F0.wireOp",EDGE,"E15.sketch_text.stroke-84"),sQuery(id+"F0.wireOp",EDGE,"E15.sketch_text.stroke-85"),sQuery(id+"F0.wireOp",EDGE,"E15.sketch_text.stroke-86"),sQuery(id+"F0.wireOp",EDGE,"E15.sketch_text.stroke-87"),sQuery(id+"F0.wireOp",EDGE,"E15.sketch_text.stroke-88"),sQuery(id+"F0.wireOp",EDGE,"E15.sketch_text.stroke-89"),sQuery(id+"F0.wireOp",EDGE,"E15.sketch_text.stroke-90"),sQuery(id+"F0.wireOp",EDGE,"E15.sketch_text.stroke-96"),sQuery(id+"F0.wireOp",EDGE,"E15.sketch_text.stroke-97"),sQuery(id+"F0.wireOp",EDGE,"E15.sketch_text.stroke-98"),sQuery(id+"F0.wireOp",EDGE,"E15.sketch_text.stroke-99"),sQuery(id+"F0.wireOp",EDGE,"E15.sketch_text.stroke-100"),sQuery(id+"F0.wireOp",EDGE,"E15.sketch_text.stroke-101"),sQuery(id+"F0.wireOp",EDGE,"E15.sketch_text.stroke-102"),sQuery(id+"F0.wireOp",EDGE,"E15.sketch_text.stroke-103"),sQuery(id+"F0.wireOp",EDGE,"E15.sketch_text.stroke-104"),sQuery(id+"F0.wireOp",EDGE,"E15.sketch_text.stroke-105"),sQuery(id+"F0.wireOp",EDGE,"E15.sketch_text.stroke-106"),sQuery(id+"F0.wireOp",EDGE,"E15.sketch_text.stroke-107"),sQuery(id+"F0.wireOp",EDGE,"E15.sketch_text.stroke-108"),sQuery(id+"F0.wireOp",EDGE,"E15.sketch_text.stroke-109"),sQuery(id+"F0.wireOp",EDGE,"E15.sketch_text.stroke-110"),sQuery(id+"F0.wireOp",EDGE,"E15.sketch_text.stroke-111"),sQuery(id+"F0.wireOp",EDGE,"E15.sketch_text.stroke-112"),sQuery(id+"F0.wireOp",EDGE,"E15.sketch_text.stroke-113"),sQuery(id+"F0.wireOp",EDGE,"E15.sketch_text.stroke-114"),sQuery(id+"F0.wireOp",EDGE,"E15.sketch_text.stroke-115"),sQuery(id+"F0.wireOp",EDGE,"E15.sketch_text.stroke-116"),sQuery(id+"F0.wireOp",EDGE,"E15.sketch_text.stroke-117"),sQuery(id+"F0.wireOp",EDGE,"E15.sketch_text.stroke-118"),sQuery(id+"F0.wireOp",EDGE,"E15.sketch_text.stroke-119"),sQuery(id+"F0.wireOp",EDGE,"E15.sketch_text.stroke-120"),sQuery(id+"F0.wireOp",EDGE,"E15.sketch_text.stroke-121"),sQuery(id+"F0.wireOp",EDGE,"E15.sketch_text.stroke-122"),sQuery(id+"F0.wireOp",EDGE,"E15.sketch_text.stroke-123"),sQuery(id+"F0.wireOp",EDGE,"E15.sketch_text.stroke-124"),sQuery(id+"F0.wireOp",EDGE,"E15.sketch_text.stroke-125"),sQuery(id+"F0.wireOp",EDGE,"E15.sketch_text.stroke-126"),sQuery(id+"F0.wireOp",EDGE,"E15.sketch_text.stroke-127"),sQuery(id+"F0.wireOp",EDGE,"E15.sketch_text.stroke-128"),sQuery(id+"F0.wireOp",EDGE,"E15.sketch_text.stroke-129"),sQuery(id+"F0.wireOp",EDGE,"E15.sketch_text.stroke-130"),sQuery(id+"F0.wireOp",EDGE,"E15.sketch_text.stroke-131"),sQuery(id+"F0.wireOp",EDGE,"E15.sketch_text.stroke-132"),sQuery(id+"F0.wireOp",EDGE,"E15.sketch_text.stroke-133"),sQuery(id+"F0.wireOp",EDGE,"E15.sketch_text.stroke-134"),sQuery(id+"F0.wireOp",EDGE,"E15.sketch_text.stroke-135"),sQuery(id+"F0.wireOp",EDGE,"E15.sketch_text.stroke-136"),sQuery(id+"F0.wireOp",EDGE,"E15.sketch_text.stroke-137"),sQuery(id+"F0.wireOp",EDGE,"E15.sketch_text.stroke-138"),sQuery(id+"F0.wireOp",EDGE,"E15.sketch_text.stroke-139"),sQuery(id+"F0.wireOp",EDGE,"E15.sketch_text.stroke-140"),sQuery(id+"F0.wireOp",EDGE,"E15.sketch_text.stroke-141"),sQuery(id+"F0.wireOp",EDGE,"E15.sketch_text.stroke-142"),sQuery(id+"F0.wireOp",EDGE,"E15.sketch_text.stroke-143"),sQuery(id+"F0.wireOp",EDGE,"E15.sketch_text.stroke-144"),sQuery(id+"F0.wireOp",EDGE,"E15.sketch_text.stroke-145"),sQuery(id+"F0.wireOp",EDGE,"E15.sketch_text.stroke-146"),sQuery(id+"F0.wireOp",EDGE,"E16"),sQuery(id+"F0.wireOp",EDGE,"E21"),sQuery(id+"F0.wireOp",EDGE,"E22"),sQuery(id+"F0.wireOp",EDGE,"E23"),sQuery(id+"F0.wireOp",EDGE,"E24"),sQuery(id+"F0.wireOp",EDGE,"E25"),sQuery(id+"F0.wireOp",EDGE,"E26"),sQuery(id+"F0.wireOp",EDGE,"E27"),sQuery(id+"F0.wireOp",EDGE,"E28"),sQuery(id+"F0.wireOp",EDGE,"E29"),sQuery(id+"F0.wireOp",EDGE,"E30"),sQuery(id+"F0.wireOp",EDGE,"E31.trimOffspring"),sQuery(id+"F0.wireOp",EDGE,"E32.trimOffspring"),sQuery(id+"F0.wireOp",EDGE,"E33.trimOffspring"),sQuery(id+"F0.wireOp",EDGE,"E34.trimOffspring"),sQuery(id+"F0.wireOp",EDGE,"E35.trimOffspring"),sQuery(id+"F0.wireOp",EDGE,"E36.trimOffspring"),sQuery(id+"F0.wireOp",EDGE,"E37.trimOffspring"),sQuery(id+"F0.wireOp",EDGE,"E38.trimOffspring"),sQuery(id+"F0.wireOp",EDGE,"E39.trimOffspring"),sQuery(id+"F0.wireOp",EDGE,"E40.trimOffspring"),sQuery(id+"F0.wireOp",EDGE,"E41.trimOffspring"),sQuery(id+"F0.wireOp",EDGE,"E42.trimOffspring"),sQuery(id+"F0.wireOp",EDGE,"E43.trimOffspring"),sQuery(id+"F0.wireOp",EDGE,"E44.trimOffspring"),sQuery(id+"F0.wireOp",EDGE,"E45.trimOffspring"),sQuery(id+"F0.wireOp",EDGE,"E46.trimOffspring"),sQuery(id+"F0.wireOp",EDGE,"E47.trimOffspring"),sQuery(id+"F0.wireOp",EDGE,"E48.trimOffspring"),sQuery(id+"F0.wireOp",EDGE,"E49.trimOffspring")])],"isStart":false}),makeQuery(id+"F3.opExtrude","CAP_FACE",FACE,{"disambiguationData":[OSD([sQuery(id+"F2.wireOp",EDGE,"E50.left"),sQuery(id+"F2.wireOp",EDGE,"E50.right"),sQuery(id+"F2.wireOp",EDGE,"E51.bottom"),sQuery(id+"F2.wireOp",EDGE,"E51.top"),sQuery(id+"F2.wireOp",EDGE,"E51.left"),sQuery(id+"F2.wireOp",EDGE,"E52.top"),sQuery(id+"F2.wireOp",EDGE,"E52.left"),sQuery(id+"F2.wireOp",EDGE,"E52.right"),sQuery(id+"F2.wireOp",EDGE,"E53.bottom"),sQuery(id+"F2.wireOp",EDGE,"E53.top"),sQuery(id+"F2.wireOp",EDGE,"E53.left"),sQuery(id+"F2.wireOp",EDGE,"E53.right")])],"isStart":true})]})});
            var sketch = newSketch(context, id + "F24", { "sketchPlane" : qUnion([Q0])});
            skText(sketch, "E61", { "text": "BOSS ", "fontName": "OpenSans-Italic.ttf"});
            const initialGuessF24  = {"E61": [-0.02414, -0.0465, 1, 0, 0.00724]};
            skSetInitialGuess(sketch, initialGuessF24);
            skSolve(sketch);
        }
        {
            var Q0;
            Q0 = qSketchRegion(id + "F24", true);
            extrude(context, id + "F25", {"entities" : qUnion([Q0]), "operationType" : NewBodyOperationType.REMOVE, "oppositeDirection" : true, "depth" : .25 * mm});
        }
    });